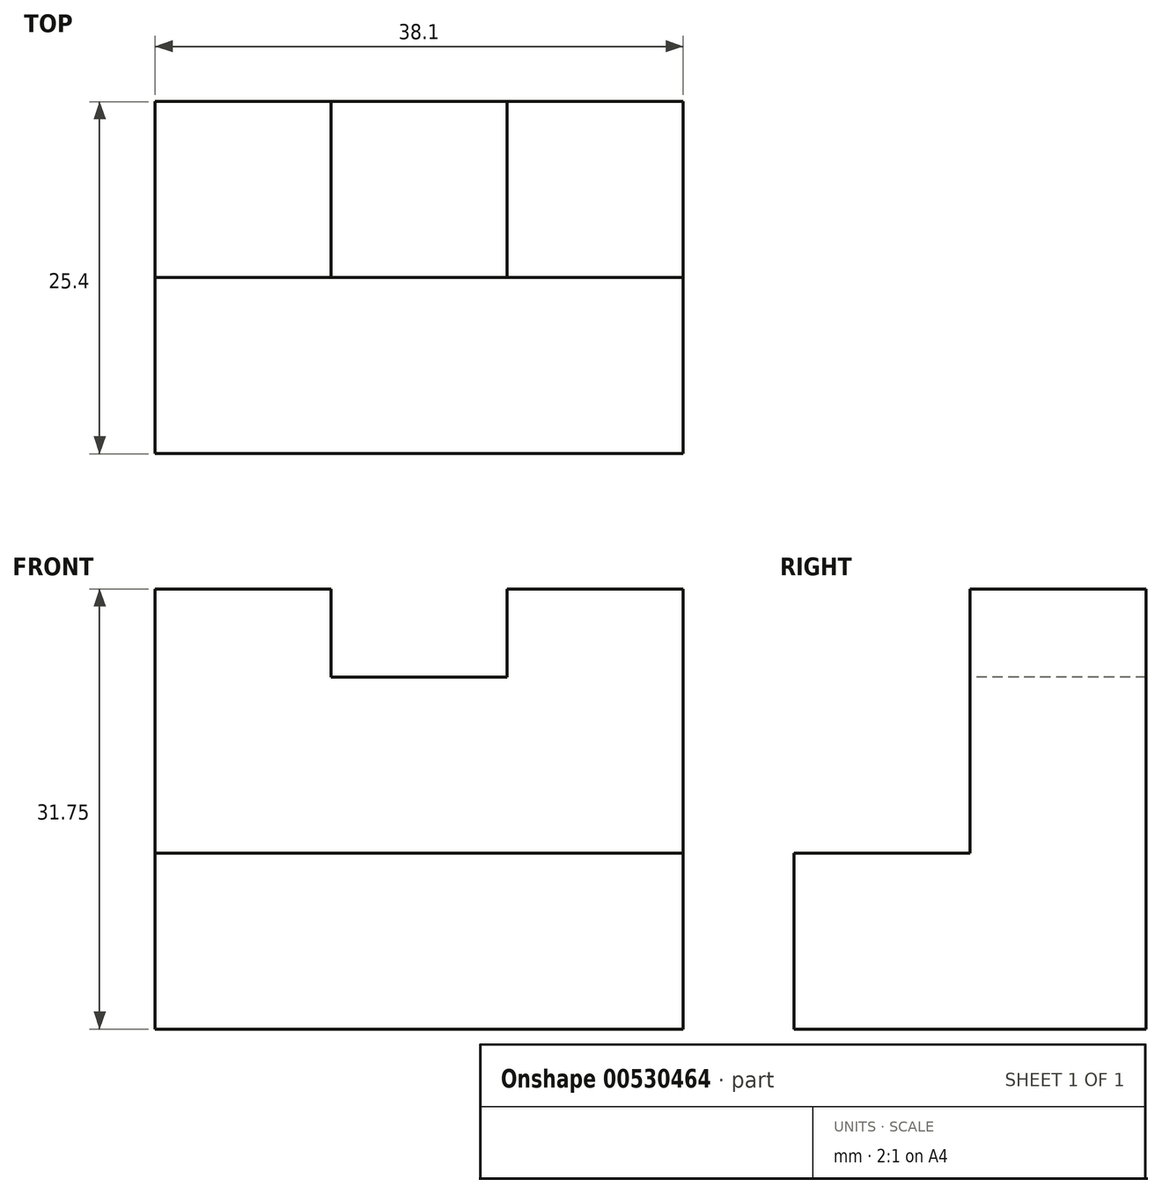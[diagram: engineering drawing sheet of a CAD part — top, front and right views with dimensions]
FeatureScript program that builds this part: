
annotation { "Feature Type Name" : "Feature", "Feature Type Description" : "" }
export const myFeature = defineFeature(function(context is Context, id is Id, definition is map)
    precondition{}
    {
        {
            var Q0;
            Q0=qCreatedBy(makeId("Right.planeOp"),FACE);
            var sketch = newSketch(context, id + "F0", { "sketchPlane" : qUnion([Q0])});
            skLineSegment(sketch, "E0", {"start": v(-19.9, 0) * mm, "end": v(-19.9, 31.75) * mm});
            skLineSegment(sketch, "E1", {"start": v(-19.9, 31.75) * mm, "end": v(-32.6, 31.75) * mm});
            skLineSegment(sketch, "E2", {"start": v(-32.6, 31.75) * mm, "end": v(-32.6, 12.7) * mm});
            skLineSegment(sketch, "E3", {"start": v(-32.6, 12.7) * mm, "end": v(-45.3, 12.7) * mm});
            skLineSegment(sketch, "E4", {"start": v(-45.3, 12.7) * mm, "end": v(-45.3, 0) * mm});
            skLineSegment(sketch, "E5", {"start": v(-45.3, 0) * mm, "end": v(-19.9, 0) * mm});
            skSolve(sketch);
        }
        {
            var Q0;
            Q0=makeQuery(id+"F0.imprint","IMPRINT",FACE,{"disambiguationData":[TD([[makeQuery(id+"F0.imprint","IMPRINT",EDGE,{"derivedFrom":sQuery(id+"F0.wireOp",EDGE,"E0")}),1.0]])]});
            extrude(context, id + "F1", {"entities" : qUnion([Q0]), "depth" : 38.1 * mm, "offsetDistance" : 25.4 * mm});
        }
        {
            var Q0;
            Q0=makeQuery(id+"F1.opExtrude","SWEPT_FACE",FACE,{"disambiguationData":[OSD([sQuery(id+"F0.wireOp",EDGE,"E2")])]});
            var sketch = newSketch(context, id + "F2", { "sketchPlane" : qUnion([Q0])});
            skLineSegment(sketch, "E6", {"start": v(12.7, 31.75) * mm, "end": v(12.7, 25.4) * mm});
            skLineSegment(sketch, "E7", {"start": v(12.7, 25.4) * mm, "end": v(25.4, 25.4) * mm});
            skLineSegment(sketch, "E8", {"start": v(25.4, 25.4) * mm, "end": v(25.4, 31.75) * mm});
            skLineSegment(sketch, "E9", {"start": v(12.7, 31.75) * mm, "end": v(25.4, 31.75) * mm});
            skSolve(sketch);
        }
        {
            var Q0;
            Q0 = qSketchRegion(id + "F2", true);
            extrude(context, id + "F3", {"entities" : qUnion([Q0]), "operationType" : NewBodyOperationType.REMOVE, "endBound" : BoundingType.THROUGH_ALL, "oppositeDirection" : true, "depth" : 25.4 * mm, "offsetDistance" : 25.4 * mm});
        }
    });
